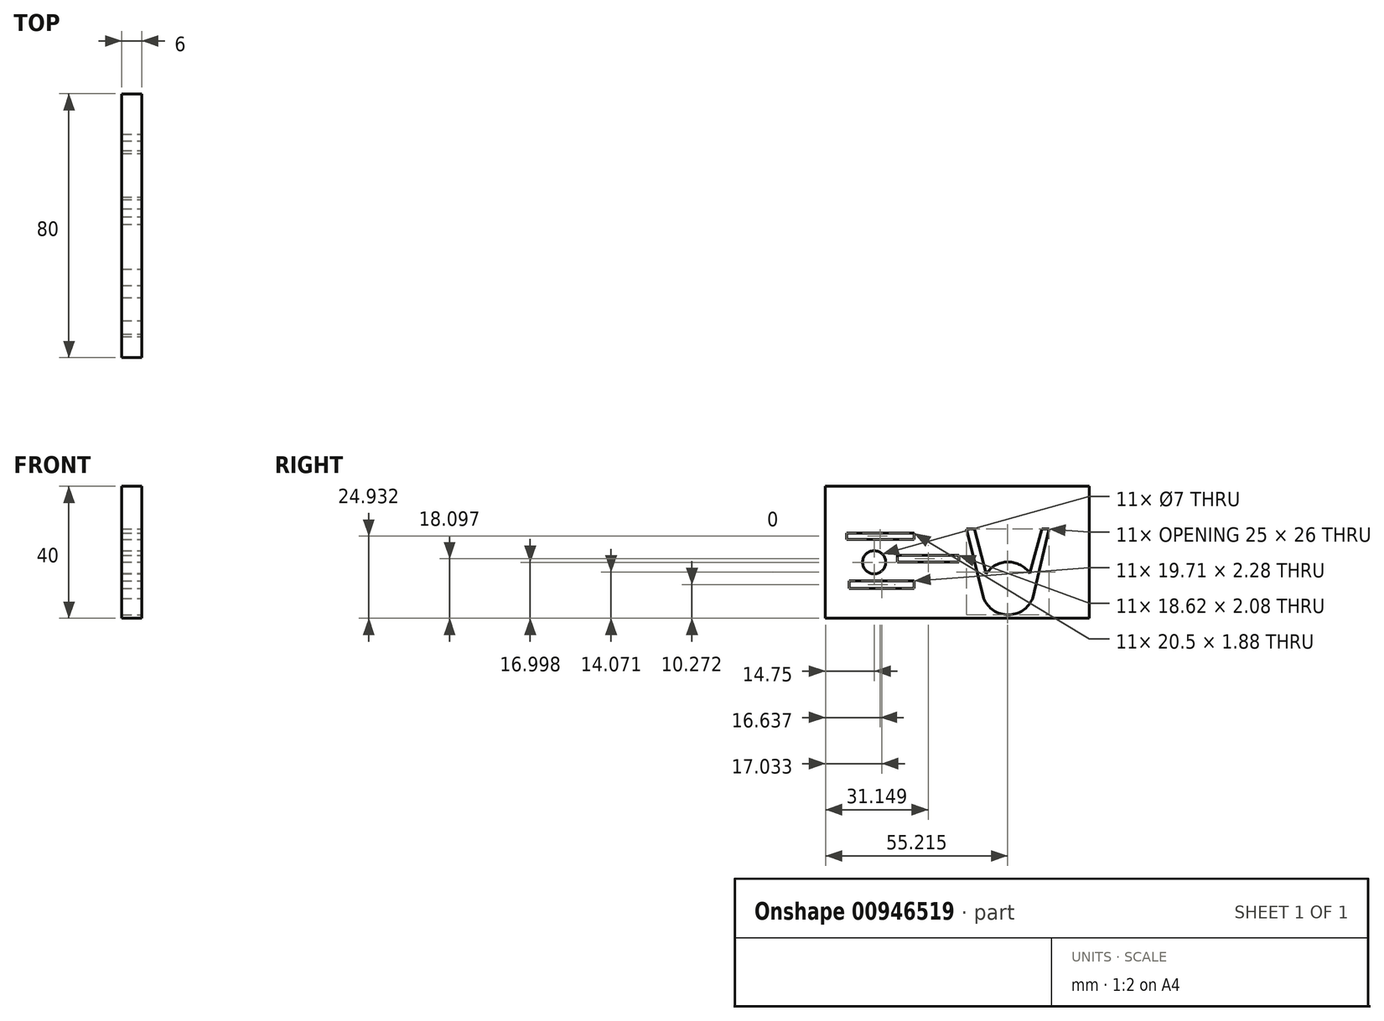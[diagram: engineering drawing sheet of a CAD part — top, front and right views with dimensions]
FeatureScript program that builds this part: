
annotation { "Feature Type Name" : "Feature", "Feature Type Description" : "" }
export const myFeature = defineFeature(function(context is Context, id is Id, definition is map)
    precondition{}
    {
        {
            var Q0;
            Q0=qCreatedBy(makeId("Right.planeOp"),FACE);
            var sketch = newSketch(context, id + "F0", { "sketchPlane" : qUnion([Q0])});
            skLineSegment(sketch, "E0.bottom", {"start": v(13.16, -2.64) * mm, "end": v(-66.84, -2.64) * mm});
            skLineSegment(sketch, "E0.top", {"start": v(13.16, 37.36) * mm, "end": v(-66.84, 37.36) * mm});
            skLineSegment(sketch, "E0.left", {"start": v(13.16, -2.64) * mm, "end": v(13.16, 37.36) * mm});
            skLineSegment(sketch, "E0.right", {"start": v(-66.84, -2.64) * mm, "end": v(-66.84, 37.36) * mm});
            skPoint(sketch, "E0.middle", {"position": v(-26.84, 17.36) * mm});
            skSolve(sketch);
        }
        {
            var Q0;
            Q0=makeQuery(id+"F0.imprint","IMPRINT",FACE,{"disambiguationData":[TD([[makeQuery(id+"F0.imprint","IMPRINT",EDGE,{"derivedFrom":sQuery(id+"F0.wireOp",EDGE,"E0.bottom")}),-1.0]])]});
            extrude(context, id + "F1", {"entities" : qUnion([Q0]), "depth" : 6 * mm, "offsetDistance" : 25 * mm});
        }
        {
            var Q0;
            Q0=makeQuery(id+"F1.opExtrude","CAP_FACE",FACE,{"disambiguationData":[OSD([sQuery(id+"F0.wireOp",EDGE,"E0.bottom"),sQuery(id+"F0.wireOp",EDGE,"E0.top"),sQuery(id+"F0.wireOp",EDGE,"E0.left"),sQuery(id+"F0.wireOp",EDGE,"E0.right")])],"isStart":false});
            var sketch = newSketch(context, id + "F2", { "sketchPlane" : qUnion([Q0])});
            skCircle(sketch, "E1", {"center": v(-52.09, 14.36) * mm, "radius": 3.5 * mm});
            skSolve(sketch);
        }
        {
            var Q0;
            Q0=makeQuery(id+"F2.imprint","IMPRINT",FACE,{"disambiguationData":[TD([[makeQuery(id+"F2.imprint","IMPRINT",EDGE,{"derivedFrom":sQuery(id+"F2.wireOp",EDGE,"E1")}),1.0]])]});
            extrude(context, id + "F3", {"entities" : qUnion([Q0]), "operationType" : NewBodyOperationType.REMOVE, "oppositeDirection" : true, "depth" : 25 * mm, "offsetDistance" : 25 * mm});
        }
        {
            var Q0;
            Q0=makeQuery(id+"F1.opExtrude","CAP_FACE",FACE,{"disambiguationData":[OSD([sQuery(id+"F0.wireOp",EDGE,"E0.bottom"),sQuery(id+"F0.wireOp",EDGE,"E0.top"),sQuery(id+"F0.wireOp",EDGE,"E0.left"),sQuery(id+"F0.wireOp",EDGE,"E0.right")])],"isStart":false});
            var sketch = newSketch(context, id + "F4", { "sketchPlane" : qUnion([Q0])});
            skLineSegment(sketch, "E2", {"start": v(-51.91, 10.86) * mm, "end": v(-21.91, 10.86) * mm});
            skCircle(sketch, "E3", {"center": v(-11.48, 6.43) * mm, "radius": 8 * mm});
            skLineSegment(sketch, "E4", {"start": v(-11.62, 14.43) * mm, "end": v(-11.62, 24.43) * mm});
            skLineSegment(sketch, "E5", {"start": v(-11.62, 24.43) * mm, "end": v(0.88, 24.43) * mm});
            skLineSegment(sketch, "E6", {"start": v(-11.62, 24.43) * mm, "end": v(-24.12, 24.43) * mm});
            skLineSegment(sketch, "E7", {"start": v(0.88, 24.43) * mm, "end": v(-4.08, 3.4) * mm});
            skLineSegment(sketch, "E8", {"start": v(-4.08, 3.4) * mm, "end": v(-18.88, 3.4) * mm});
            skLineSegment(sketch, "E9", {"start": v(-18.88, 3.4) * mm, "end": v(-24.12, 24.43) * mm});
            skLineSegment(sketch, "E10", {"start": v(-1.19, 24.43) * mm, "end": v(-4.89, 10.97) * mm});
            skLineSegment(sketch, "E11", {"start": v(-21.65, 24.43) * mm, "end": v(-17.94, 10.27) * mm});
            skSolve(sketch);
        }
        {
            var Q0;
            {var subQ4=sQuery(id+"F4.wireOp",EDGE,"E8");Q0=makeQuery(id+"F4.imprint","IMPRINT",FACE,{"disambiguationData":[TD([[makeQuery(id+"F4.imprint","IMPRINT",EDGE,{"derivedFrom":subQ4}),-1.0]])]});}
            var Q1;
            {var subQ0=sQuery(id+"F4.wireOp",EDGE,"E8");Q1=makeQuery(id+"F4.imprint","IMPRINT",FACE,{"disambiguationData":[TD([[makeQuery(id+"F4.imprint","IMPRINT",EDGE,{"derivedFrom":subQ0}),1.0]])]});}
            var Q2;
            {var subQ0=sQuery(id+"F4.wireOp",EDGE,"E11");var subQ1=sQuery(id+"F4.wireOp",EDGE,"E3");var subQ2=makeQuery(id+"F4.imprint","INTERSECT",VERTEX,{"derivedFrom":[subQ1,subQ0]});Q2=makeQuery(id+"F4.imprint","IMPRINT",FACE,{"disambiguationData":[TD([[makeQuery(id+"F4.imprint","IMPRINT",EDGE,{"disambiguationData":[TD([[subQ2,-1.0]])],"derivedFrom":subQ1}),-1.0]])]});}
            var Q3;
            {var subQ0=sQuery(id+"F4.wireOp",EDGE,"E10");Q3=makeQuery(id+"F4.imprint","IMPRINT",FACE,{"disambiguationData":[TD([[makeQuery(id+"F4.imprint","IMPRINT",EDGE,{"derivedFrom":subQ0}),1.0]])]});}
            extrude(context, id + "F5", {"entities" : qUnion([Q0, Q1, Q2, Q3]), "operationType" : NewBodyOperationType.REMOVE, "oppositeDirection" : true, "depth" : 25 * mm, "offsetDistance" : 25 * mm});
        }
        {
            var Q0;
            Q0=makeQuery(id+"F1.opExtrude","CAP_FACE",FACE,{"disambiguationData":[OSD([sQuery(id+"F0.wireOp",EDGE,"E0.bottom"),sQuery(id+"F0.wireOp",EDGE,"E0.top"),sQuery(id+"F0.wireOp",EDGE,"E0.left"),sQuery(id+"F0.wireOp",EDGE,"E0.right")])],"isStart":false});
            var sketch = newSketch(context, id + "F6", { "sketchPlane" : qUnion([Q0])});
            skLineSegment(sketch, "E12.bottom", {"start": v(-60.46, 23.23) * mm, "end": v(-39.95, 23.23) * mm});
            skLineSegment(sketch, "E12.top", {"start": v(-60.46, 21.35) * mm, "end": v(-39.95, 21.35) * mm});
            skLineSegment(sketch, "E12.left", {"start": v(-60.46, 23.23) * mm, "end": v(-60.46, 21.35) * mm});
            skLineSegment(sketch, "E12.right", {"start": v(-39.95, 23.23) * mm, "end": v(-39.95, 21.35) * mm});
            skLineSegment(sketch, "E13.bottom", {"start": v(-59.66, 8.77) * mm, "end": v(-39.95, 8.77) * mm});
            skLineSegment(sketch, "E13.top", {"start": v(-59.66, 6.5) * mm, "end": v(-39.95, 6.5) * mm});
            skLineSegment(sketch, "E13.left", {"start": v(-59.66, 8.77) * mm, "end": v(-59.66, 6.5) * mm});
            skLineSegment(sketch, "E13.right", {"start": v(-39.95, 8.77) * mm, "end": v(-39.95, 6.5) * mm});
            skLineSegment(sketch, "E14.bottom", {"start": v(-45, 16.5) * mm, "end": v(-26.38, 16.5) * mm});
            skLineSegment(sketch, "E14.top", {"start": v(-45, 14.42) * mm, "end": v(-26.38, 14.42) * mm});
            skLineSegment(sketch, "E14.left", {"start": v(-45, 16.5) * mm, "end": v(-45, 14.42) * mm});
            skLineSegment(sketch, "E14.right", {"start": v(-26.38, 16.5) * mm, "end": v(-26.38, 14.42) * mm});
            skSolve(sketch);
        }
        {
            var Q0;
            Q0=makeQuery(id+"F6.imprint","IMPRINT",FACE,{"disambiguationData":[TD([[makeQuery(id+"F6.imprint","IMPRINT",EDGE,{"derivedFrom":sQuery(id+"F6.wireOp",EDGE,"E12.bottom")}),-1.0]])]});
            var Q1;
            Q1=makeQuery(id+"F6.imprint","IMPRINT",FACE,{"disambiguationData":[TD([[makeQuery(id+"F6.imprint","IMPRINT",EDGE,{"derivedFrom":sQuery(id+"F6.wireOp",EDGE,"E14.bottom")}),-1.0]])]});
            var Q2;
            Q2=makeQuery(id+"F6.imprint","IMPRINT",FACE,{"disambiguationData":[TD([[makeQuery(id+"F6.imprint","IMPRINT",EDGE,{"derivedFrom":sQuery(id+"F6.wireOp",EDGE,"E13.bottom")}),-1.0]])]});
            extrude(context, id + "F7", {"entities" : qUnion([Q0, Q1, Q2]), "operationType" : NewBodyOperationType.REMOVE, "oppositeDirection" : true, "depth" : 25 * mm, "offsetDistance" : 25 * mm});
        }
    });
